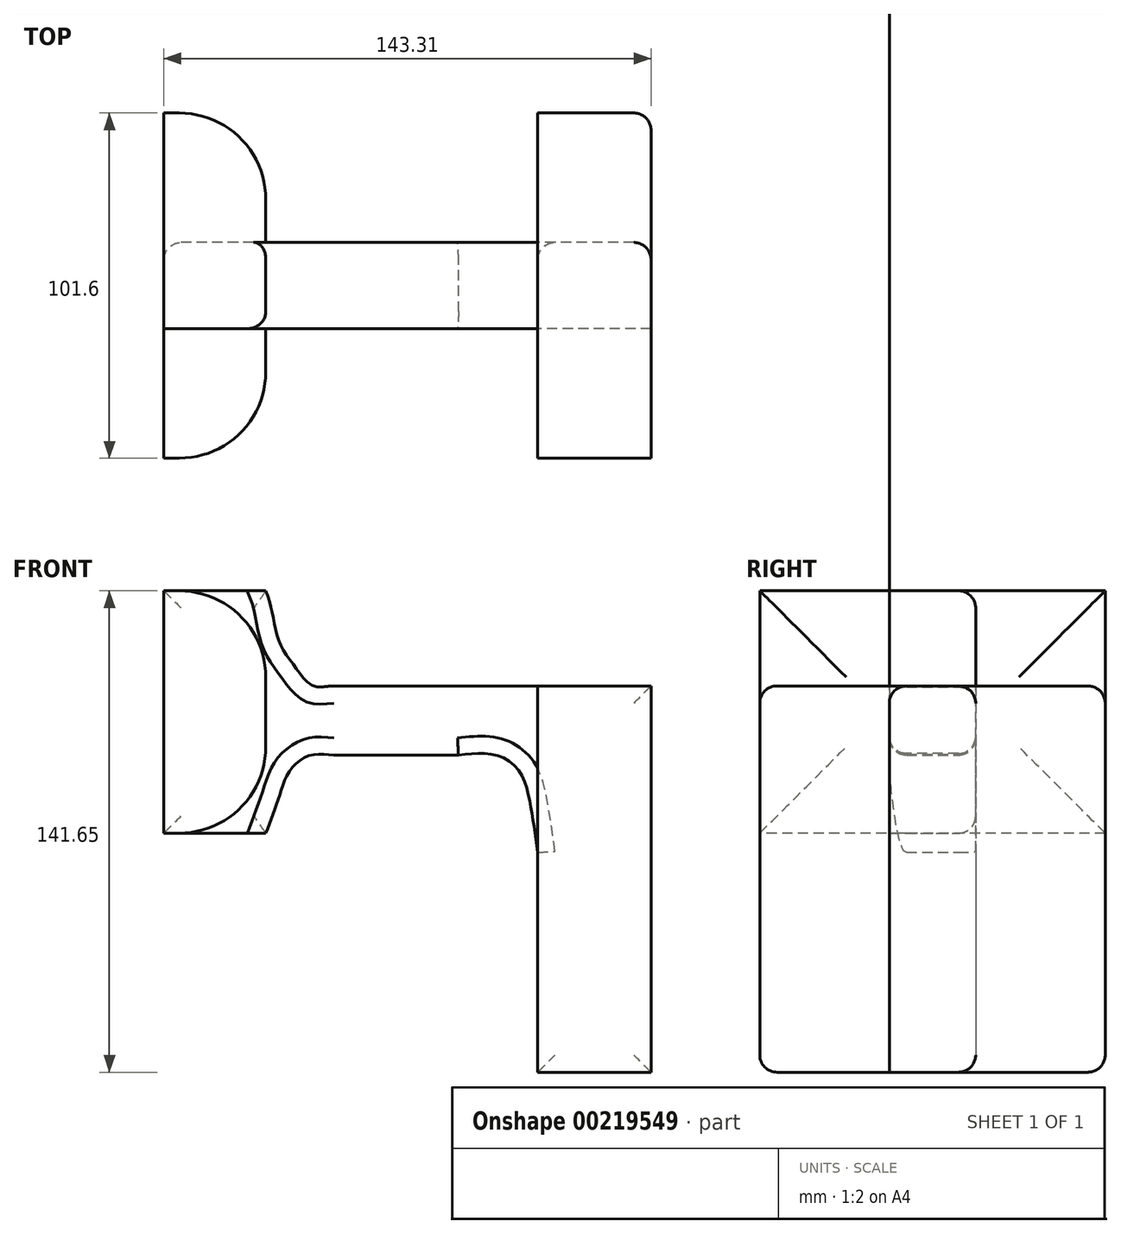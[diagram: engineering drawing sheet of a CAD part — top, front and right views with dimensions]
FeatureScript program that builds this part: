
annotation { "Feature Type Name" : "Feature", "Feature Type Description" : "" }
export const myFeature = defineFeature(function(context is Context, id is Id, definition is map)
    precondition{}
    {
        {
            var Q0;
            Q0=qCreatedBy(makeId("Front.planeOp"),FACE);
            var sketch = newSketch(context, id + "F0", { "sketchPlane" : qUnion([Q0])});
            skLineSegment(sketch, "E0.bottom", {"start": v(16.66, 56.83) * mm, "end": v(-16.66, 56.83) * mm});
            skLineSegment(sketch, "E0.top", {"start": v(16.66, -56.83) * mm, "end": v(-16.66, -56.83) * mm});
            skLineSegment(sketch, "E0.left", {"start": v(16.66, 56.83) * mm, "end": v(16.66, -56.83) * mm});
            skLineSegment(sketch, "E0.right", {"start": v(-16.66, 56.83) * mm, "end": v(-16.66, -56.83) * mm});
            skPoint(sketch, "E0.middle", {"position": v(0, 0) * mm});
            skLineSegment(sketch, "E1.bottom", {"start": v(-96.65, 13.5) * mm, "end": v(-126.65, 13.5) * mm});
            skLineSegment(sketch, "E1.top", {"start": v(-96.65, 84.82) * mm, "end": v(-126.65, 84.82) * mm});
            skLineSegment(sketch, "E1.left", {"start": v(-96.65, 13.5) * mm, "end": v(-96.65, 84.82) * mm});
            skLineSegment(sketch, "E1.right", {"start": v(-126.65, 13.5) * mm, "end": v(-126.65, 84.82) * mm});
            skPoint(sketch, "E1.middle", {"position": v(-111.65, 49.16) * mm});
            skLineSegment(sketch, "E2", {"start": v(-76.66, 36.5) * mm, "end": v(-40, 36.5) * mm});
            skLineSegment(sketch, "E3", {"start": v(-76.69, 56.83) * mm, "end": v(-16.66, 56.83) * mm});
            skFitSpline(sketch, "E4", {"points": [v(-40, 36.5) * mm, v(-29, 36.5) * mm, v(-22.66, 32.5) * mm, v(-19.66, 25.83) * mm, v(-16.66, 7.83) * mm], "startDerivative": vector(45.88, 4.88) * mm, "endDerivative": vector(8.52, -61.5) * mm});
            skFitSpline(sketch, "E5", {"points": [v(-76.66, 36.5) * mm, v(-83.32, 36.5) * mm, v(-89.65, 31.83) * mm, v(-92.32, 25.5) * mm, v(-96.65, 13.5) * mm], "startDerivative": vector(-30.16, 0) * mm, "endDerivative": vector(-15.8, -41.94) * mm});
            skFitSpline(sketch, "E6", {"points": [v(-76.69, 56.83) * mm, v(-82.66, 56.83) * mm, v(-88.32, 62.82) * mm, v(-92.99, 70.5) * mm, v(-96.65, 84.82) * mm], "startDerivative": vector(-30.77, 0) * mm, "endDerivative": vector(-19.41, 44.84) * mm});
            skSolve(sketch);
        }
        {
            var Q0;
            {var subQ1=sQuery(id+"F0.wireOp",EDGE,"E0.bottom");Q0=makeQuery(id+"F0.imprint","IMPRINT",FACE,{"disambiguationData":[TD([[makeQuery(id+"F0.imprint","IMPRINT",EDGE,{"derivedFrom":subQ1}),1.0]])]});}
            var Q1;
            Q1=makeQuery(id+"F0.imprint","IMPRINT",FACE,{"disambiguationData":[TD([[makeQuery(id+"F0.imprint","IMPRINT",EDGE,{"derivedFrom":sQuery(id+"F0.wireOp",EDGE,"E1.bottom")}),-1.0]])]});
            extrude(context, id + "F1", {"entities" : qUnion([Q0, Q1]), "endBound" : BoundingType.SYMMETRIC, "oppositeDirection" : true, "depth" : 101.6 * mm});
        }
        {
            var Q0;
            Q0 = qSketchRegion(id + "F0", true);
            extrude(context, id + "F2", {"entities" : qUnion([Q0]), "endBound" : BoundingType.SYMMETRIC, "depth" : 25.4 * mm});
        }
        {
            var Q0;
            Q0=makeQuery(id+"F1.opExtrude","CAP_EDGE",EDGE,{"disambiguationData":[OSD([sQuery(id+"F0.wireOp",EDGE,"E0.bottom")])],"isStart":true});
            var Q1;
            Q1=makeQuery(id+"F1.opExtrude","CAP_EDGE",EDGE,{"disambiguationData":[OSD([sQuery(id+"F0.wireOp",EDGE,"E0.top")])],"isStart":true});
            var Q2;
            Q2=makeQuery(id+"F1.opExtrude","CAP_EDGE",EDGE,{"disambiguationData":[OSD([sQuery(id+"F0.wireOp",EDGE,"E0.top")])],"isStart":false});
            var Q3;
            Q3=makeQuery(id+"F1.opExtrude","CAP_EDGE",EDGE,{"disambiguationData":[OSD([sQuery(id+"F0.wireOp",EDGE,"E0.bottom")])],"isStart":false});
            var Q4;
            Q4=makeQuery(id+"F2.opExtrude","CAP_EDGE",EDGE,{"disambiguationData":[OSD([sQuery(id+"F0.wireOp",EDGE,"E0.bottom"),sQuery(id+"F0.wireOp",EDGE,"E3")])],"isStart":false});
            var Q5;
            Q5=makeQuery(id+"F2.opExtrude","CAP_EDGE",EDGE,{"disambiguationData":[OSD([sQuery(id+"F0.wireOp",EDGE,"E2")])],"isStart":true});
            var Q6;
            Q6=makeQuery(id+"F2.opExtrude","CAP_EDGE",EDGE,{"disambiguationData":[OSD([sQuery(id+"F0.wireOp",EDGE,"E4")])],"isStart":true});
            var Q7;
            Q7=makeQuery(id+"F2.opExtrude","CAP_EDGE",EDGE,{"disambiguationData":[OSD([sQuery(id+"F0.wireOp",EDGE,"E4")])],"isStart":false});
            var Q8;
            Q8=makeQuery(id+"F2.opExtrude","CAP_EDGE",EDGE,{"disambiguationData":[OSD([sQuery(id+"F0.wireOp",EDGE,"E2")])],"isStart":false});
            var Q9;
            Q9=makeQuery(id+"F2.opExtrude","CAP_FACE",FACE,{"disambiguationData":[OSD([sQuery(id+"F0.wireOp",EDGE,"E0.bottom"),sQuery(id+"F0.wireOp",EDGE,"E0.top"),sQuery(id+"F0.wireOp",EDGE,"E0.left"),sQuery(id+"F0.wireOp",EDGE,"E0.right"),sQuery(id+"F0.wireOp",EDGE,"E1.bottom"),sQuery(id+"F0.wireOp",EDGE,"E1.top"),sQuery(id+"F0.wireOp",EDGE,"E1.right"),sQuery(id+"F0.wireOp",EDGE,"E2"),sQuery(id+"F0.wireOp",EDGE,"E3"),sQuery(id+"F0.wireOp",EDGE,"E4"),sQuery(id+"F0.wireOp",EDGE,"E5"),sQuery(id+"F0.wireOp",EDGE,"E6")])],"isStart":true});
            var Q10;
            Q10=makeQuery(id+"F1.opExtrude","CAP_EDGE",EDGE,{"disambiguationData":[OSD([sQuery(id+"F0.wireOp",EDGE,"E0.left")])],"isStart":false});
            fillet(context, id + "F3", {"entities" : qUnion([Q0, Q1, Q2, Q3, Q4, Q5, Q6, Q7, Q8, Q9, Q10]), "radius" : 5.08 * mm, "tangentPropagation" : true, "allowEdgeOverflow" : false});
        }
        {
            var Q0;
            Q0=makeQuery(id+"F1.opExtrude","SWEPT_EDGE",EDGE,{"disambiguationData":[OSD([sQuery(id+"F0.wireOp",EDGE,"E1.top"),sQuery(id+"F0.wireOp",EDGE,"E1.left"),sQuery(id+"F0.wireOp",EDGE,"E6")])]});
            var Q1;
            Q1=makeQuery(id+"F1.opExtrude","CAP_EDGE",EDGE,{"disambiguationData":[OSD([sQuery(id+"F0.wireOp",EDGE,"E1.left")])],"isStart":true});
            var Q2;
            Q2=makeQuery(id+"F1.opExtrude","CAP_EDGE",EDGE,{"disambiguationData":[OSD([sQuery(id+"F0.wireOp",EDGE,"E1.left")])],"isStart":false});
            var Q3;
            Q3=makeQuery(id+"F1.opExtrude","SWEPT_EDGE",EDGE,{"disambiguationData":[OSD([sQuery(id+"F0.wireOp",EDGE,"E1.bottom"),sQuery(id+"F0.wireOp",EDGE,"E1.left"),sQuery(id+"F0.wireOp",EDGE,"E5")])]});
            fillet(context, id + "F4", {"entities" : qUnion([Q0, Q1, Q2, Q3]), "radius" : 25.4 * mm, "tangentPropagation" : true, "allowEdgeOverflow" : false});
        }
    });
